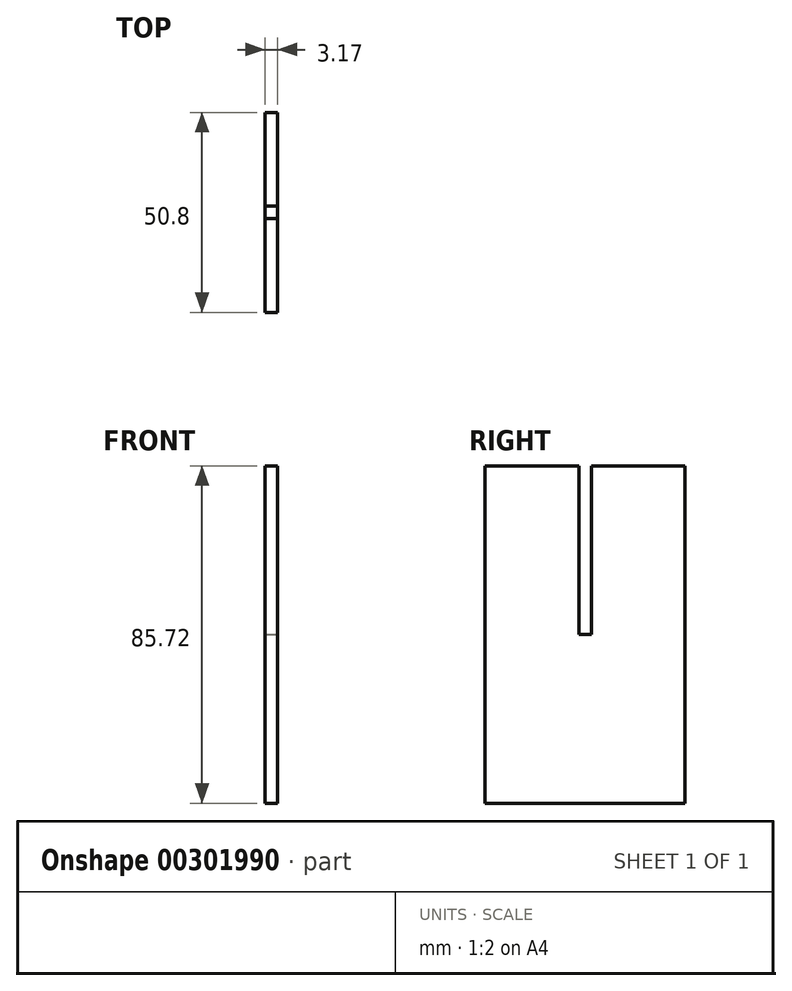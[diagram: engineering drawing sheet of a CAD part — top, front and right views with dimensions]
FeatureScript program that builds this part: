
annotation { "Feature Type Name" : "Feature", "Feature Type Description" : "" }
export const myFeature = defineFeature(function(context is Context, id is Id, definition is map)
    precondition{}
    {
        {
            var Q0;
            Q0=qCreatedBy(makeId("Right.planeOp"),FACE);
            var sketch = newSketch(context, id + "F0", { "sketchPlane" : qUnion([Q0])});
            skLineSegment(sketch, "E0.bottom", {"start": v(-25.4, 42.86) * mm, "end": v(25.4, 42.86) * mm});
            skLineSegment(sketch, "E0.top", {"start": v(-25.4, -42.86) * mm, "end": v(25.4, -42.86) * mm});
            skLineSegment(sketch, "E0.left", {"start": v(-25.4, 42.86) * mm, "end": v(-25.4, -42.86) * mm});
            skLineSegment(sketch, "E0.right", {"start": v(25.4, 42.86) * mm, "end": v(25.4, -42.86) * mm});
            skPoint(sketch, "E0.middle", {"position": v(0, 0) * mm});
            skSolve(sketch);
        }
        {
            var Q0;
            Q0 = qSketchRegion(id + "F0", true);
            extrude(context, id + "F1", {"entities" : qUnion([Q0]), "depth" : 3.17 * mm});
        }
        {
            var Q0;
            Q0=makeQuery(id+"F1.opExtrude","CAP_FACE",FACE,{"disambiguationData":[OSD([sQuery(id+"F0.wireOp",EDGE,"E0.bottom"),sQuery(id+"F0.wireOp",EDGE,"E0.top"),sQuery(id+"F0.wireOp",EDGE,"E0.left"),sQuery(id+"F0.wireOp",EDGE,"E0.right")])],"isStart":false});
            var sketch = newSketch(context, id + "F2", { "sketchPlane" : qUnion([Q0])});
            skLineSegment(sketch, "E1.bottom", {"start": v(-1.59, 0) * mm, "end": v(1.59, 0) * mm});
            skLineSegment(sketch, "E1.top", {"start": v(-1.59, 42.86) * mm, "end": v(1.59, 42.86) * mm});
            skLineSegment(sketch, "E1.left", {"start": v(-1.59, 0) * mm, "end": v(-1.59, 42.86) * mm});
            skLineSegment(sketch, "E1.right", {"start": v(1.59, 0) * mm, "end": v(1.59, 42.86) * mm});
            skPoint(sketch, "E1.middle", {"position": v(0, 21.43) * mm});
            skPoint(sketch, "E1.middle.positionSnap0", {"position": v(0, 42.86) * mm});
            skPoint(sketch, "E1.centerSnap0", {"position": v(0, 42.86) * mm});
            skSolve(sketch);
        }
        {
            var Q0;
            Q0 = qSketchRegion(id + "F2", true);
            extrude(context, id + "F3", {"entities" : qUnion([Q0]), "operationType" : NewBodyOperationType.REMOVE, "oppositeDirection" : true, "depth" : 3.17 * mm});
        }
    });
